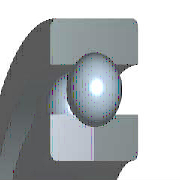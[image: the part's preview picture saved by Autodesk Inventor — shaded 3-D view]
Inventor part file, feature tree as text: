
AUTODESK INVENTOR PART (.ipt)
format: ipt  version: 2015 (Build 190159000, 159)  size: 298,496 bytes
history: native  units: mm (DEFAULTED — no unit token found)
features: sketch x1, other x1, pattern_circular x1
ambient origin geometry x8: Origin, YZ Plane, XZ Plane, XY Plane, X Axis, Y Axis, Z Axis, Center Point
bodies: Body (feature_tree)
feature tree (3):
  sketch  "Sketch"  dims[d9=90.0deg d0=0.3mm d12=90.0deg d1=80.0mm d2=360.0deg d3=4.16mm d4=0.0mm d5=0.0mm d6=0.0mm d7=12.0mm d8=28.0mm d10=8.0mm d11=20.0mm d13=17.216mm d15=22.784mm d16=0.0mm d17=0.0mm]
  other  "Ball"
  pattern_circular  "Balls"  [2 undecoded]
note: 2 required parameter values undecoded (feature->parameter linkage not recoverable at this tier; creation-order binding heuristic only, values carry confidence <= 0.55)
